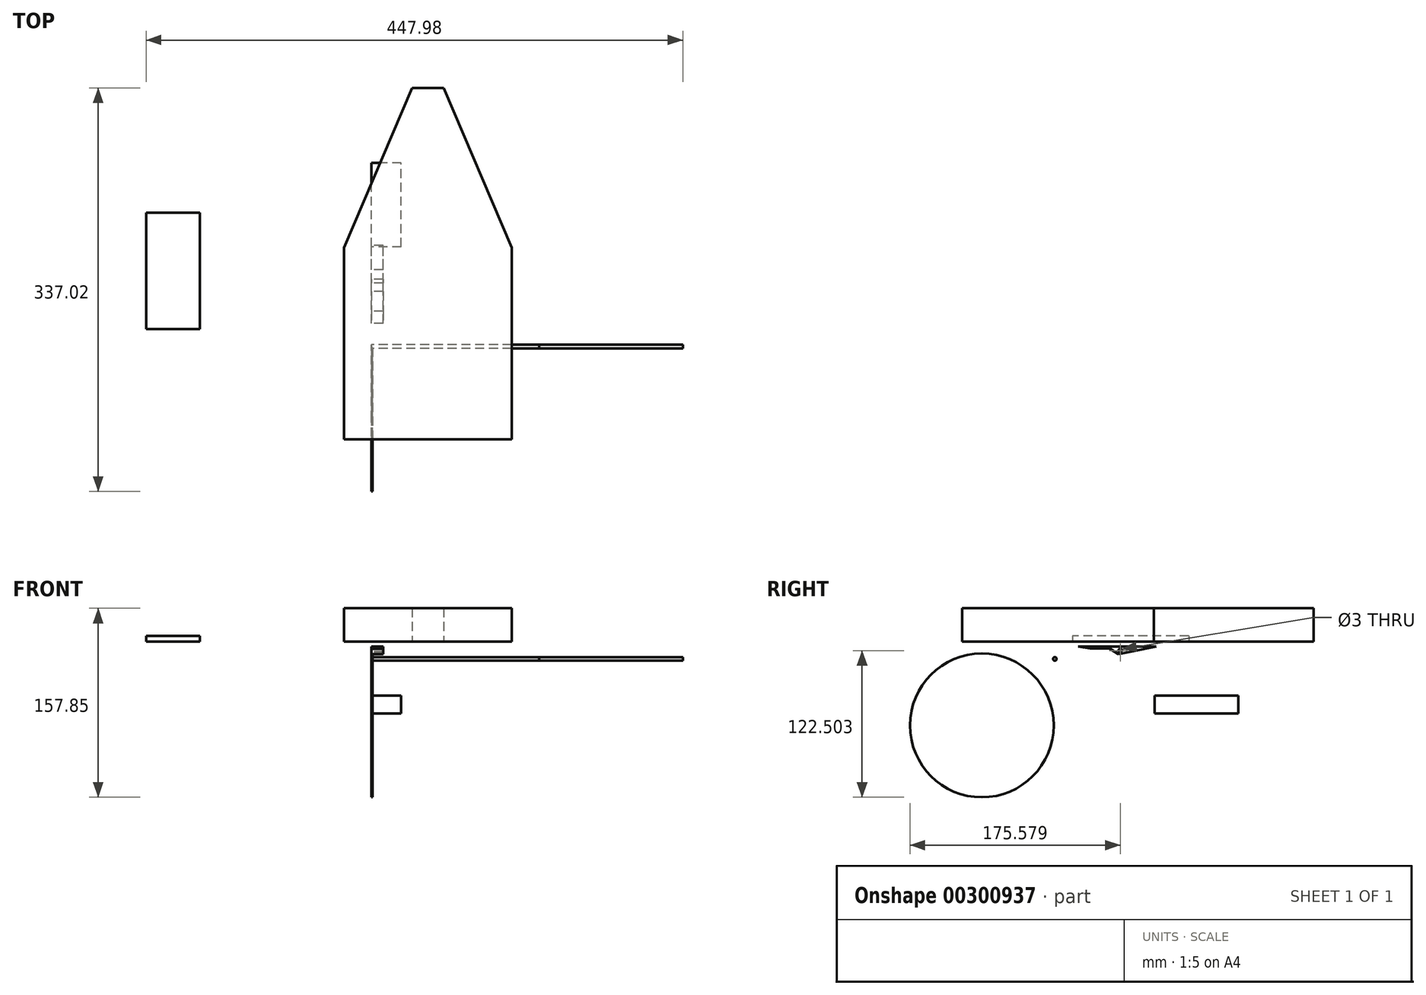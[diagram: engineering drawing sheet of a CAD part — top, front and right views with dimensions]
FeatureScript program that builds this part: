
annotation { "Feature Type Name" : "Feature", "Feature Type Description" : "" }
export const myFeature = defineFeature(function(context is Context, id is Id, definition is map)
    precondition{}
    {
        {
            var Q0;
            Q0=qCreatedBy(makeId("Top.planeOp"),FACE);
            var sketch = newSketch(context, id + "F0", { "sketchPlane" : qUnion([Q0])});
            skLineSegment(sketch, "E0.bottom", {"start": v(-22.78, 32.65) * mm, "end": v(117.22, 32.65) * mm});
            skLineSegment(sketch, "E0.top", {"start": v(-22.78, -127.35) * mm, "end": v(117.22, -127.35) * mm});
            skLineSegment(sketch, "E0.left", {"start": v(-22.78, 32.65) * mm, "end": v(-22.78, -127.35) * mm});
            skLineSegment(sketch, "E0.right", {"start": v(117.22, 32.65) * mm, "end": v(117.22, -127.35) * mm});
            skLineSegment(sketch, "E1", {"start": v(-22.78, 32.65) * mm, "end": v(33.93, 166.1) * mm});
            skLineSegment(sketch, "E2", {"start": v(33.93, 166.1) * mm, "end": v(60.5, 166.1) * mm});
            skLineSegment(sketch, "E3", {"start": v(60.5, 166.1) * mm, "end": v(117.22, 32.65) * mm});
            skLineSegment(sketch, "E4", {"start": v(47.22, 166.1) * mm, "end": v(47.22, 32.65) * mm});
            skLineSegment(sketch, "E5.bottom", {"start": v(-187.98, 61.8) * mm, "end": v(-142.98, 61.8) * mm});
            skLineSegment(sketch, "E5.top", {"start": v(-187.98, -35.2) * mm, "end": v(-142.98, -35.2) * mm});
            skLineSegment(sketch, "E5.left", {"start": v(-187.98, 61.8) * mm, "end": v(-187.98, -35.2) * mm});
            skLineSegment(sketch, "E5.right", {"start": v(-142.98, 61.8) * mm, "end": v(-142.98, -35.2) * mm});
            skSolve(sketch);
        }
        {
            var Q0;
            Q0=makeQuery(id+"F0.imprint","IMPRINT",FACE,{"disambiguationData":[TD([[makeQuery(id+"F0.imprint","IMPRINT",EDGE,{"derivedFrom":sQuery(id+"F0.wireOp",EDGE,"E0.top")}),1.0]])]});
            var Q1;
            {var subQ0=sQuery(id+"F0.wireOp",EDGE,"E1");Q1=makeQuery(id+"F0.imprint","IMPRINT",FACE,{"disambiguationData":[TD([[makeQuery(id+"F0.imprint","IMPRINT",EDGE,{"derivedFrom":subQ0}),-1.0]])]});}
            var Q2;
            {var subQ0=sQuery(id+"F0.wireOp",EDGE,"E3");Q2=makeQuery(id+"F0.imprint","IMPRINT",FACE,{"disambiguationData":[TD([[makeQuery(id+"F0.imprint","IMPRINT",EDGE,{"derivedFrom":subQ0}),-1.0]])]});}
            extrude(context, id + "F1", {"entities" : qUnion([Q0, Q1, Q2]), "depth" : 28 * mm});
        }
        {
            var Q0;
            Q0=qCreatedBy(makeId("Right.planeOp"),FACE);
            var sketch = newSketch(context, id + "F2", { "sketchPlane" : qUnion([Q0])});
            skLineSegment(sketch, "E6", {"start": v(-30.53, -4.05) * mm, "end": v(-20.53, -4.05) * mm});
            skLineSegment(sketch, "E7", {"start": v(34.47, -4.05) * mm, "end": v(21.78, -6.51) * mm});
            skLineSegment(sketch, "E8", {"start": v(21.78, -6.51) * mm, "end": v(21.78, -6.51) * mm});
            skLineSegment(sketch, "E9", {"start": v(-4, -6.04) * mm, "end": v(3.12, -10.36) * mm});
            skLineSegment(sketch, "E10", {"start": v(-4, -6.04) * mm, "end": v(-8.2, -5.9) * mm});
            skLineSegment(sketch, "E11", {"start": v(-8.2, -5.9) * mm, "end": v(-10.54, -5.82) * mm});
            skCircle(sketch, "E12", {"center": v(4.65, -7.35) * mm, "radius": 1.5 * mm});
            skCircle(sketch, "E13", {"center": v(-49.97, -14.33) * mm, "radius": 1.5 * mm});
            skCircle(sketch, "E14", {"center": v(-110.93, -69.85) * mm, "radius": 60 * mm});
            skLineSegment(sketch, "E15", {"start": v(14.27, -7.97) * mm, "end": v(21.78, -6.51) * mm});
            skLineSegment(sketch, "E16", {"start": v(3.12, -10.36) * mm, "end": v(14.27, -7.97) * mm});
            skLineSegment(sketch, "E17", {"start": v(-10.54, -5.82) * mm, "end": v(-20.53, -5.49) * mm});
            skLineSegment(sketch, "E18", {"start": v(-20.53, -5.49) * mm, "end": v(-30.53, -4.05) * mm});
            skLineSegment(sketch, "E19", {"start": v(-20.53, -4.05) * mm, "end": v(34.47, -4.05) * mm});
            skLineSegment(sketch, "E20.bottom", {"start": v(33.31, -44.84) * mm, "end": v(103.31, -44.84) * mm});
            skLineSegment(sketch, "E20.top", {"start": v(33.31, -59.84) * mm, "end": v(103.31, -59.84) * mm});
            skLineSegment(sketch, "E20.left", {"start": v(33.31, -44.84) * mm, "end": v(33.31, -59.84) * mm});
            skLineSegment(sketch, "E20.right", {"start": v(103.31, -44.84) * mm, "end": v(103.31, -59.84) * mm});
            skSolve(sketch);
        }
        {
            var Q0;
            Q0=makeQuery(id+"F2.imprint","IMPRINT",FACE,{"disambiguationData":[TD([[makeQuery(id+"F2.imprint","IMPRINT",EDGE,{"derivedFrom":sQuery(id+"F2.wireOp",EDGE,"E14")}),1.0]])]});
            extrude(context, id + "F3", {"entities" : qUnion([Q0]), "depth" : 1 * mm});
        }
        {
            var Q0;
            Q0=makeQuery(id+"F2.imprint","IMPRINT",FACE,{"disambiguationData":[TD([[makeQuery(id+"F2.imprint","IMPRINT",EDGE,{"derivedFrom":sQuery(id+"F2.wireOp",EDGE,"E13")}),1.0]])]});
            extrude(context, id + "F4", {"entities" : qUnion([Q0]), "depth" : 260 * mm});
        }
        {
            var Q0;
            Q0=makeQuery(id+"F2.imprint","IMPRINT",FACE,{"disambiguationData":[TD([[makeQuery(id+"F2.imprint","IMPRINT",EDGE,{"derivedFrom":sQuery(id+"F2.wireOp",EDGE,"E6")}),-1.0]])]});
            extrude(context, id + "F5", {"entities" : qUnion([Q0]), "depth" : 10 * mm});
        }
        {
            var Q0;
            Q0=makeQuery(id+"F2.imprint","IMPRINT",FACE,{"disambiguationData":[TD([[makeQuery(id+"F2.imprint","IMPRINT",EDGE,{"derivedFrom":sQuery(id+"F2.wireOp",EDGE,"E20.bottom")}),-1.0]])]});
            extrude(context, id + "F6", {"entities" : qUnion([Q0]), "depth" : 25 * mm});
        }
        {
            var Q0;
            Q0=makeQuery(id+"F0.imprint","IMPRINT",FACE,{"disambiguationData":[TD([[makeQuery(id+"F0.imprint","IMPRINT",EDGE,{"derivedFrom":sQuery(id+"F0.wireOp",EDGE,"E5.bottom")}),-1.0]])]});
            extrude(context, id + "F7", {"entities" : qUnion([Q0]), "depth" : 5 * mm});
        }
        {
            var Q0;
            Q0=makeQuery(id+"F2.imprint","IMPRINT",FACE,{"disambiguationData":[TD([[makeQuery(id+"F2.imprint","IMPRINT",EDGE,{"derivedFrom":sQuery(id+"F2.wireOp",EDGE,"E13")}),1.0]])]});
            extrude(context, id + "F8", {"entities" : qUnion([Q0]), "depth" : 140 * mm});
        }
    });
